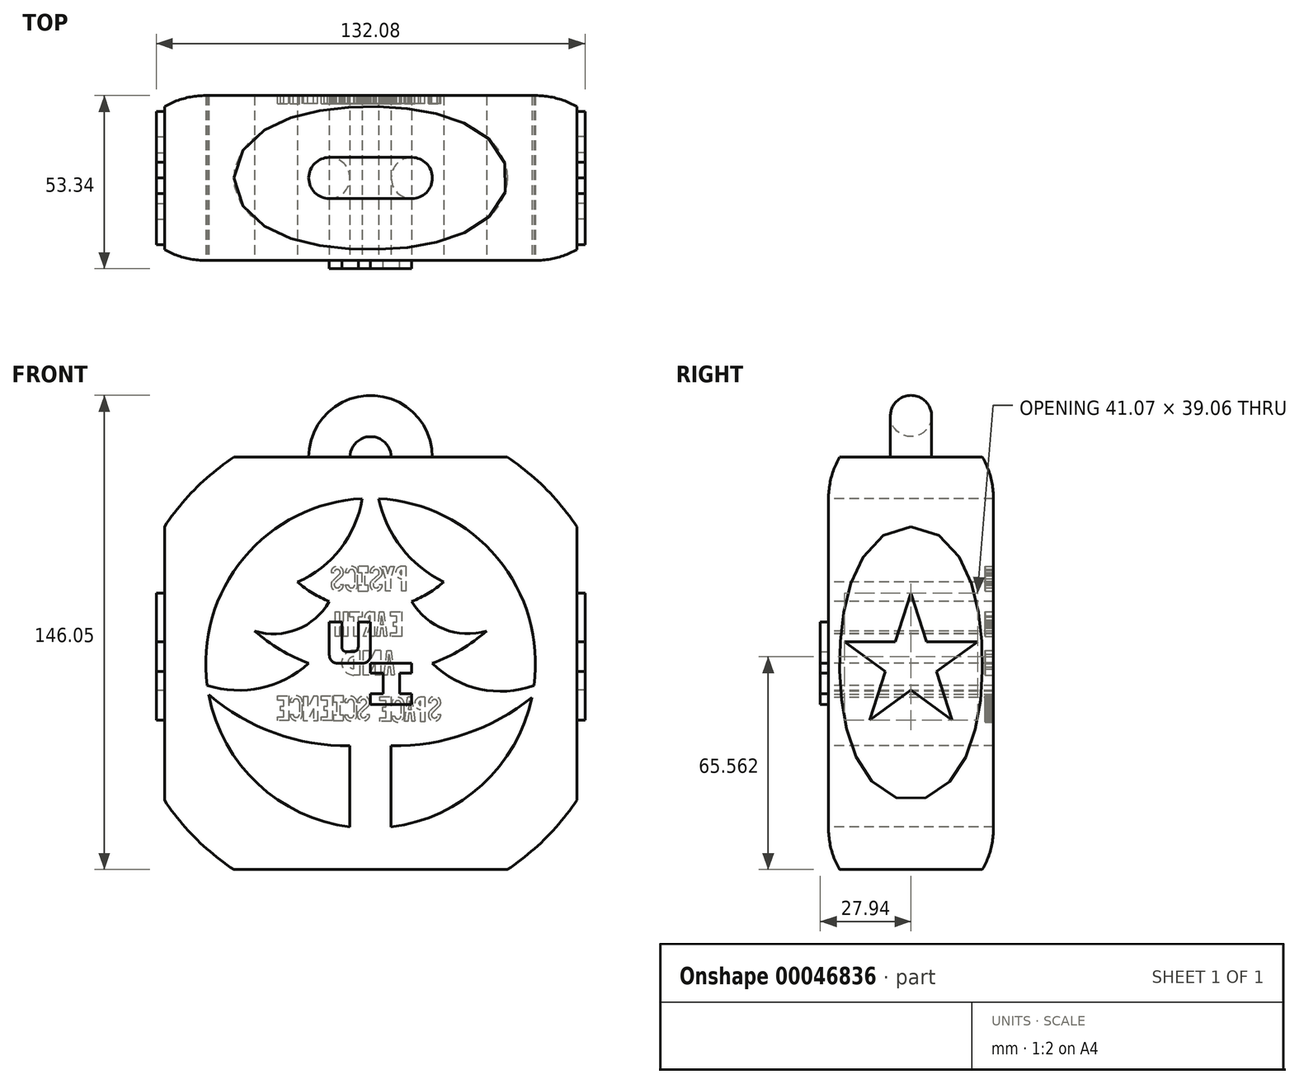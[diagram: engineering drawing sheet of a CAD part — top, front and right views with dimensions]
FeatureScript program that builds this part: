
annotation { "Feature Type Name" : "Feature", "Feature Type Description" : "" }
export const myFeature = defineFeature(function(context is Context, id is Id, definition is map)
    precondition{}
    {
        {
            var Q0;
            Q0=qCreatedBy(makeId("Top.planeOp"),FACE);
            var sketch = newSketch(context, id + "F0", { "sketchPlane" : qUnion([Q0])});
            skLineSegment(sketch, "E0", {"start": v(0, 0) * mm, "end": v(0, 25.4) * mm});
            skLineSegment(sketch, "E1", {"start": v(0, 0) * mm, "end": v(0, -25.4) * mm});
            skLineSegment(sketch, "E2", {"start": v(0, 25.4) * mm, "end": v(50.8, 25.4) * mm});
            skLineSegment(sketch, "E3", {"start": v(50.8, 25.4) * mm, "end": v(50.8, -25.4) * mm});
            skLineSegment(sketch, "E4", {"start": v(50.8, -25.4) * mm, "end": v(0, -25.4) * mm});
            skArc(sketch, "E5", {"start": v(50.8, -25.4) * mm, "mid": v(76.2, 0) * mm, "end": v(50.8, 25.4) * mm});
            skSolve(sketch);
        }
        {
            var Q0;
            Q0 = qSketchRegion(id + "F0", true);
            var Q1;
            Q1=sQuery(id+"F0.wireOp",EDGE,"E0");
            revolve(context, id + "F1", {"entities" : qUnion([Q0]), "axis" : qUnion([Q1]), "revolveType" : RevolveType.FULL});
        }
        {
            var Q0;
            Q0=makeQuery(id+"F1.opRevolve","SWEPT_FACE",FACE,{"disambiguationData":[OSD([sQuery(id+"F0.wireOp",EDGE,"E4")])]});
            var sketch = newSketch(context, id + "F2", { "sketchPlane" : qUnion([Q0])});
            skLineSegment(sketch, "E6", {"start": v(-6.35, -48.26) * mm, "end": v(-6.35, -25.4) * mm});
            skLineSegment(sketch, "E7", {"start": v(6.35, -48.26) * mm, "end": v(6.35, -25.4) * mm});
            skArc(sketch, "E8", {"start": v(19.05, 0) * mm, "mid": v(33.72, -7.94) * mm, "end": v(50.35, -6.75) * mm});
            skArc(sketch, "E9", {"start": v(-50.35, -6.75) * mm, "mid": v(-33.8, -7.59) * mm, "end": v(-19.05, 0) * mm});
            skArc(sketch, "E10", {"start": v(-35.73, 9.97) * mm, "mid": v(-27.84, 4.23) * mm, "end": v(-19.05, 0) * mm});
            skArc(sketch, "E11", {"start": v(12.7, 19.05) * mm, "mid": v(22.65, 10.55) * mm, "end": v(35.73, 9.97) * mm});
            skArc(sketch, "E12", {"start": v(-35.73, 9.97) * mm, "mid": v(-22.62, 10.46) * mm, "end": v(-12.7, 19.05) * mm});
            skArc(sketch, "E13", {"start": v(-22.52, 25.06) * mm, "mid": v(-17.86, 21.64) * mm, "end": v(-12.7, 19.05) * mm});
            skArc(sketch, "E14.trimOffspring", {"start": v(12.7, 19.05) * mm, "mid": v(17.86, 21.64) * mm, "end": v(22.52, 25.06) * mm});
            skArc(sketch, "E15.trimOffspring", {"start": v(19.05, 0) * mm, "mid": v(27.84, 4.23) * mm, "end": v(35.73, 9.97) * mm});
            skLineSegment(sketch, "E16", {"start": v(-6.35, -48.26) * mm, "end": v(-6.35, -50.4) * mm});
            skLineSegment(sketch, "E17", {"start": v(6.35, -48.26) * mm, "end": v(6.35, -50.4) * mm});
            skArc(sketch, "E18", {"start": v(-22.52, 25.06) * mm, "mid": v(-9.27, 35.35) * mm, "end": v(-2.6, 50.73) * mm});
            skArc(sketch, "E19", {"start": v(2.53, 50.74) * mm, "mid": v(9.54, 35.57) * mm, "end": v(22.52, 25.06) * mm});
            skCircle(sketch, "E20", {"center": v(0, 0) * mm, "radius": 50.8 * mm});
            skArc(sketch, "E21", {"start": v(-49.88, -9.63) * mm, "mid": v(-29.55, -21.47) * mm, "end": v(-6.35, -25.4) * mm});
            skArc(sketch, "E22", {"start": v(6.35, -25.4) * mm, "mid": v(29.33, -21.72) * mm, "end": v(49.7, -10.48) * mm});
            skSolve(sketch);
        }
        {
            var Q0;
            Q0=makeQuery(id+"F2.imprint","IMPRINT",FACE,{"disambiguationData":[TD([[makeQuery(id+"F2.imprint","IMPRINT",EDGE,{"derivedFrom":sQuery(id+"F2.wireOp",EDGE,"E6")}),1.0]])]});
            extrude(context, id + "F3", {"entities" : qUnion([Q0]), "operationType" : NewBodyOperationType.REMOVE, "oppositeDirection" : true, "depth" : 145.88 * mm});
        }
        {
            var Q0;
            {var subQ2=sQuery(id+"F2.wireOp",EDGE,"E8");Q0=makeQuery(id+"F2.imprint","IMPRINT",FACE,{"disambiguationData":[TD([[makeQuery(id+"F2.imprint","IMPRINT",EDGE,{"derivedFrom":subQ2}),1.0]])]});}
            extrude(context, id + "F4", {"entities" : qUnion([Q0]), "operationType" : NewBodyOperationType.REMOVE, "oppositeDirection" : true, "depth" : 112.84 * mm});
        }
        {
            var Q0;
            {var subQ1=sQuery(id+"F2.wireOp",EDGE,"E9");Q0=makeQuery(id+"F2.imprint","IMPRINT",FACE,{"disambiguationData":[TD([[makeQuery(id+"F2.imprint","IMPRINT",EDGE,{"derivedFrom":subQ1}),1.0]])]});}
            extrude(context, id + "F5", {"entities" : qUnion([Q0]), "operationType" : NewBodyOperationType.REMOVE, "oppositeDirection" : true, "depth" : 60.8 * mm});
        }
        {
            var Q0;
            Q0=makeQuery(id+"F2.imprint","IMPRINT",FACE,{"disambiguationData":[TD([[makeQuery(id+"F2.imprint","IMPRINT",EDGE,{"derivedFrom":sQuery(id+"F2.wireOp",EDGE,"E7")}),-1.0]])]});
            extrude(context, id + "F6", {"entities" : qUnion([Q0]), "operationType" : NewBodyOperationType.REMOVE, "oppositeDirection" : true, "depth" : 63.8 * mm});
        }
        {
            var Q0;
            Q0=makeQuery(id+"F1.opRevolve","SWEPT_FACE",FACE,{"disambiguationData":[OSD([sQuery(id+"F0.wireOp",EDGE,"E4")])]});
            var sketch = newSketch(context, id + "F7", { "sketchPlane" : qUnion([Q0])});
            skLineSegment(sketch, "E23", {"start": v(0, 0) * mm, "end": v(0, -63.5) * mm});
            skPoint(sketch, "E23.endSnap0", {"position": v(0, -50.8) * mm});
            skLineSegment(sketch, "E24", {"start": v(0, -63.5) * mm, "end": v(-69.31, -63.5) * mm});
            skLineSegment(sketch, "E25", {"start": v(-69.31, -63.5) * mm, "end": v(-69.31, -78.3) * mm});
            skLineSegment(sketch, "E26", {"start": v(-69.31, -78.3) * mm, "end": v(74.16, -78.3) * mm});
            skLineSegment(sketch, "E27", {"start": v(74.16, -78.3) * mm, "end": v(74.16, -63.5) * mm});
            skLineSegment(sketch, "E28", {"start": v(74.16, -63.5) * mm, "end": v(0, -63.5) * mm});
            skLineSegment(sketch, "E29", {"start": v(0, 0) * mm, "end": v(-63.5, 0) * mm});
            skLineSegment(sketch, "E30", {"start": v(0, 0) * mm, "end": v(63.5, 0) * mm});
            skLineSegment(sketch, "E31", {"start": v(0, 0) * mm, "end": v(0, 63.5) * mm});
            skLineSegment(sketch, "E32", {"start": v(-63.5, 0) * mm, "end": v(-63.5, 51.43) * mm});
            skLineSegment(sketch, "E33", {"start": v(-63.5, 51.43) * mm, "end": v(-82.24, 51.43) * mm});
            skLineSegment(sketch, "E34", {"start": v(-82.24, 51.43) * mm, "end": v(-82.24, -30.11) * mm});
            skLineSegment(sketch, "E35", {"start": v(-82.24, -30.11) * mm, "end": v(-82.24, -49.77) * mm});
            skLineSegment(sketch, "E36", {"start": v(-82.24, -49.77) * mm, "end": v(-63.5, -49.77) * mm});
            skLineSegment(sketch, "E37", {"start": v(-63.5, -49.77) * mm, "end": v(-63.5, 0) * mm});
            skLineSegment(sketch, "E38", {"start": v(63.5, 0) * mm, "end": v(63.5, 56.35) * mm});
            skLineSegment(sketch, "E39", {"start": v(63.5, 56.35) * mm, "end": v(89.23, 56.35) * mm});
            skLineSegment(sketch, "E40", {"start": v(89.23, 56.35) * mm, "end": v(89.23, -52.38) * mm});
            skLineSegment(sketch, "E41", {"start": v(89.23, -52.38) * mm, "end": v(63.5, -52.38) * mm});
            skLineSegment(sketch, "E42", {"start": v(63.5, -52.38) * mm, "end": v(63.5, 0) * mm});
            skLineSegment(sketch, "E43", {"start": v(0, 63.5) * mm, "end": v(48.36, 63.5) * mm});
            skLineSegment(sketch, "E44", {"start": v(48.36, 63.5) * mm, "end": v(48.36, 80.87) * mm});
            skLineSegment(sketch, "E45", {"start": v(48.36, 80.87) * mm, "end": v(-58.03, 80.87) * mm});
            skLineSegment(sketch, "E46", {"start": v(-58.03, 80.87) * mm, "end": v(-58.03, 63.5) * mm});
            skLineSegment(sketch, "E47", {"start": v(-58.03, 63.5) * mm, "end": v(0, 63.5) * mm});
            skSolve(sketch);
        }
        {
            var Q0;
            Q0 = qSketchRegion(id + "F7", true);
            extrude(context, id + "F8", {"entities" : qUnion([Q0]), "operationType" : NewBodyOperationType.REMOVE, "oppositeDirection" : true, "depth" : 73.08 * mm});
        }
        {
            var Q0;
            Q0 = qSketchRegion(id + "F7", true);
            extrude(context, id + "F9", {"entities" : qUnion([Q0]), "operationType" : NewBodyOperationType.REMOVE, "oppositeDirection" : true, "depth" : 74.54 * mm});
        }
        {
            var Q0;
            Q0=makeQuery(id+"F8.boolean.opBoolean","COPY",FACE,{"derivedFrom":makeQuery(id+"F8.opExtrude","SWEPT_FACE",FACE,{"disambiguationData":[OSD([sQuery(id+"F7.wireOp",EDGE,"E43"),sQuery(id+"F7.wireOp",EDGE,"E47")])]})});
            var sketch = newSketch(context, id + "F10", { "sketchPlane" : qUnion([Q0])});
            skLineSegment(sketch, "E48", {"start": v(0, 0) * mm, "end": v(12.7, 0) * mm});
            skLineSegment(sketch, "E49", {"start": v(0, 0) * mm, "end": v(0, 12.46) * mm});
            skLineSegment(sketch, "E50", {"start": v(0, 0) * mm, "end": v(-12.7, 0) * mm});
            skCircle(sketch, "E51", {"center": v(12.7, 0) * mm, "radius": 6.35 * mm});
            skCircle(sketch, "E52", {"center": v(-12.7, 0) * mm, "radius": 6.35 * mm});
            skSolve(sketch);
        }
        {
            var Q0;
            Q0=makeQuery(id+"F10.imprint","IMPRINT",FACE,{"disambiguationData":[TD([[makeQuery(id+"F10.imprint","IMPRINT",EDGE,{"derivedFrom":sQuery(id+"F10.wireOp",EDGE,"E52")}),1.0]])]});
            var Q1;
            Q1=sQuery(id+"F10.wireOp",EDGE,"E49");
            revolve(context, id + "F11", {"operationType" : NewBodyOperationType.ADD, "entities" : qUnion([Q0]), "axis" : qUnion([Q1]), "revolveType" : RevolveType.ONE_DIRECTION, "angle" : 180 * degree});
        }
        {
            var Q0;
            Q0=makeQuery(id+"F8.boolean.opBoolean","COPY",FACE,{"derivedFrom":makeQuery(id+"F8.opExtrude","SWEPT_FACE",FACE,{"disambiguationData":[OSD([sQuery(id+"F7.wireOp",EDGE,"E32"),sQuery(id+"F7.wireOp",EDGE,"E37")])]})});
            var sketch = newSketch(context, id + "F12", { "sketchPlane" : qUnion([Q0])});
            skLineSegment(sketch, "E53", {"start": v(0, 21.59) * mm, "end": v(-4.85, 6.67) * mm});
            skLineSegment(sketch, "E54", {"start": v(20.53, 6.67) * mm, "end": v(7.84, -2.55) * mm});
            skLineSegment(sketch, "E55", {"start": v(-20.53, 6.67) * mm, "end": v(-4.85, 6.67) * mm});
            skLineSegment(sketch, "E56", {"start": v(-20.53, 6.67) * mm, "end": v(-7.84, -2.55) * mm});
            skLineSegment(sketch, "E57", {"start": v(12.7, -17.47) * mm, "end": v(7.84, -2.55) * mm});
            skLineSegment(sketch, "E58.trimOffspring", {"start": v(4.85, 6.67) * mm, "end": v(20.53, 6.67) * mm});
            skLineSegment(sketch, "E59.trimOffspring", {"start": v(4.85, 6.67) * mm, "end": v(0, 21.59) * mm});
            skLineSegment(sketch, "E60.trimOffspring", {"start": v(0, -8.25) * mm, "end": v(-12.7, -17.47) * mm});
            skLineSegment(sketch, "E61.trimOffspring", {"start": v(0, -8.25) * mm, "end": v(12.7, -17.47) * mm});
            skLineSegment(sketch, "E62.trimOffspring", {"start": v(-7.84, -2.55) * mm, "end": v(-12.7, -17.47) * mm});
            skSolve(sketch);
        }
        {
            var Q0;
            Q0 = qSketchRegion(id + "F12", true);
            extrude(context, id + "F13", {"entities" : qUnion([Q0]), "operationType" : NewBodyOperationType.ADD, "depth" : 2.54 * mm});
        }
        {
            var Q0;
            Q0=makeQuery(id+"F8.boolean.opBoolean","COPY",FACE,{"derivedFrom":makeQuery(id+"F8.opExtrude","SWEPT_FACE",FACE,{"disambiguationData":[OSD([sQuery(id+"F7.wireOp",EDGE,"E38"),sQuery(id+"F7.wireOp",EDGE,"E42")])]})});
            var sketch = newSketch(context, id + "F14", { "sketchPlane" : qUnion([Q0])});
            skCircle(sketch, "E63.cCircle", {"center": v(0, 0) * mm, "radius": 21.59 * mm, "construction": true});
            skLineSegment(sketch, "E63.0", {"start": v(0, 21.59) * mm, "end": v(20.53, 6.67) * mm});
            skLineSegment(sketch, "E63.1", {"start": v(20.53, 6.67) * mm, "end": v(12.7, -17.47) * mm});
            skLineSegment(sketch, "E63.2", {"start": v(12.7, -17.47) * mm, "end": v(-12.7, -17.47) * mm});
            skLineSegment(sketch, "E63.3", {"start": v(-12.7, -17.47) * mm, "end": v(-20.53, 6.67) * mm});
            skLineSegment(sketch, "E63.4", {"start": v(-20.53, 6.67) * mm, "end": v(0, 21.59) * mm});
            skLineSegment(sketch, "E64", {"start": v(-12.7, -17.47) * mm, "end": v(-7.84, -2.55) * mm});
            skLineSegment(sketch, "E65", {"start": v(12.7, -17.47) * mm, "end": v(7.84, -2.55) * mm});
            skLineSegment(sketch, "E66", {"start": v(-20.53, 6.67) * mm, "end": v(-4.85, 6.67) * mm});
            skLineSegment(sketch, "E67", {"start": v(20.53, 6.67) * mm, "end": v(7.84, -2.55) * mm});
            skLineSegment(sketch, "E68", {"start": v(-20.53, 6.67) * mm, "end": v(-7.84, -2.55) * mm});
            skLineSegment(sketch, "E69.trimOffspring", {"start": v(4.85, 6.67) * mm, "end": v(20.53, 6.67) * mm});
            skLineSegment(sketch, "E70.trimOffspring", {"start": v(4.85, 6.67) * mm, "end": v(0, 21.59) * mm});
            skLineSegment(sketch, "E71.trimOffspring", {"start": v(0, -8.25) * mm, "end": v(-12.7, -17.47) * mm});
            skLineSegment(sketch, "E72.trimOffspring", {"start": v(0, -8.25) * mm, "end": v(12.7, -17.47) * mm});
            skLineSegment(sketch, "E73.trimOffspring", {"start": v(-4.85, 6.67) * mm, "end": v(0, 21.59) * mm});
            skSolve(sketch);
        }
        {
            var Q0;
            Q0=makeQuery(id+"F14.imprint","IMPRINT",FACE,{"disambiguationData":[TD([[makeQuery(id+"F14.imprint","IMPRINT",EDGE,{"derivedFrom":sQuery(id+"F14.wireOp",EDGE,"E64")}),-1.0]])]});
            extrude(context, id + "F15", {"entities" : qUnion([Q0]), "operationType" : NewBodyOperationType.ADD, "depth" : 2.54 * mm});
        }
        {
            var Q0;
            Q0=makeQuery(id+"F1.opRevolve","SWEPT_FACE",FACE,{"disambiguationData":[OSD([sQuery(id+"F0.wireOp",EDGE,"E4")])]});
            var sketch = newSketch(context, id + "F16", { "sketchPlane" : qUnion([Q0])});
            skLineSegment(sketch, "E74", {"start": v(-2.54, 0) * mm, "end": v(-10.16, 0) * mm});
            skLineSegment(sketch, "E75", {"start": v(-12.7, 2.54) * mm, "end": v(-12.7, 12.7) * mm});
            skLineSegment(sketch, "E76", {"start": v(-12.7, 12.7) * mm, "end": v(-8.9, 12.7) * mm});
            skLineSegment(sketch, "E77", {"start": v(-8.9, 12.7) * mm, "end": v(-8.9, 5.08) * mm});
            skLineSegment(sketch, "E78", {"start": v(-7.37, 3.56) * mm, "end": v(-5.33, 3.56) * mm});
            skLineSegment(sketch, "E79", {"start": v(-3.8, 5.08) * mm, "end": v(-3.8, 12.7) * mm});
            skLineSegment(sketch, "E80", {"start": v(-3.81, 12.7) * mm, "end": v(0, 12.7) * mm});
            skLineSegment(sketch, "E81", {"start": v(0, 12.7) * mm, "end": v(0, 2.54) * mm});
            skPoint(sketch, "E82.visualSharp", {"position": v(-8.9, 3.56) * mm});
            skArc(sketch, "E82.filletArc", {"start": v(-8.9, 5.08) * mm, "mid": v(-8.44, 4) * mm, "end": v(-7.37, 3.56) * mm});
            skPoint(sketch, "E83.visualSharp", {"position": v(-3.8, 3.56) * mm});
            skArc(sketch, "E83.filletArc", {"start": v(-5.33, 3.56) * mm, "mid": v(-4.26, 4) * mm, "end": v(-3.8, 5.08) * mm});
            skPoint(sketch, "E84.visualSharp", {"position": v(-12.7, 0) * mm});
            skArc(sketch, "E84.filletArc", {"start": v(-12.7, 2.54) * mm, "mid": v(-11.96, 0.74) * mm, "end": v(-10.16, 0) * mm});
            skPoint(sketch, "E85.visualSharp", {"position": v(0, 0) * mm});
            skArc(sketch, "E85.filletArc", {"start": v(-2.54, 0) * mm, "mid": v(-0.74, 0.74) * mm, "end": v(0, 2.54) * mm});
            skLineSegment(sketch, "E86", {"start": v(0, 0) * mm, "end": v(12.7, 0) * mm});
            skLineSegment(sketch, "E87", {"start": v(0, 0) * mm, "end": v(0, -3.05) * mm});
            skLineSegment(sketch, "E88", {"start": v(0, -3.05) * mm, "end": v(3.8, -3.05) * mm});
            skLineSegment(sketch, "E89", {"start": v(3.81, -3.05) * mm, "end": v(3.81, -9.4) * mm});
            skLineSegment(sketch, "E90", {"start": v(3.81, -9.4) * mm, "end": v(0, -9.4) * mm});
            skLineSegment(sketch, "E91", {"start": v(0, -9.4) * mm, "end": v(0, -12.7) * mm});
            skLineSegment(sketch, "E92", {"start": v(0, -12.7) * mm, "end": v(12.7, -12.7) * mm});
            skLineSegment(sketch, "E93", {"start": v(12.7, -12.7) * mm, "end": v(12.7, -9.4) * mm});
            skLineSegment(sketch, "E94", {"start": v(12.7, -9.4) * mm, "end": v(8.9, -9.4) * mm});
            skLineSegment(sketch, "E95", {"start": v(8.9, -9.4) * mm, "end": v(8.9, -3.05) * mm});
            skLineSegment(sketch, "E96", {"start": v(8.9, -3.05) * mm, "end": v(12.7, -3.05) * mm});
            skLineSegment(sketch, "E97", {"start": v(12.7, -3.05) * mm, "end": v(12.7, 0) * mm});
            skSolve(sketch);
        }
        {
            var Q0;
            Q0 = qSketchRegion(id + "F16", true);
            extrude(context, id + "F17", {"entities" : qUnion([Q0]), "operationType" : NewBodyOperationType.ADD, "depth" : 2.54 * mm});
        }
        {
            var Q0;
            Q0=makeQuery(id+"F1.opRevolve","SWEPT_FACE",FACE,{"disambiguationData":[OSD([sQuery(id+"F0.wireOp",EDGE,"E2")])]});
            var sketch = newSketch(context, id + "F18", { "sketchPlane" : qUnion([Q0])});
            skLineSegment(sketch, "E98", {"start": v(-10.91, 29.9) * mm, "end": v(-10.91, 22.27) * mm});
            skLineSegment(sketch, "E99", {"start": v(-10.91, 22.27) * mm, "end": v(-9.64, 22.27) * mm});
            skLineSegment(sketch, "E100", {"start": v(-9.64, 22.27) * mm, "end": v(-9.64, 26.08) * mm});
            skLineSegment(sketch, "E101", {"start": v(-10.91, 29.9) * mm, "end": v(-9.64, 29.9) * mm});
            skArc(sketch, "E102", {"start": v(-9.64, 26.08) * mm, "mid": v(-7.74, 27.99) * mm, "end": v(-9.64, 29.9) * mm});
            skLineSegment(sketch, "E103", {"start": v(-9.64, 27.35) * mm, "end": v(-9.64, 28.62) * mm});
            skArc(sketch, "E104", {"start": v(-9.64, 27.35) * mm, "mid": v(-9, 27.99) * mm, "end": v(-9.64, 28.62) * mm});
            skLineSegment(sketch, "E105", {"start": v(-7.24, 29.9) * mm, "end": v(-6.15, 26.08) * mm});
            skLineSegment(sketch, "E106", {"start": v(-6.15, 26.08) * mm, "end": v(-6.15, 22.27) * mm});
            skLineSegment(sketch, "E107", {"start": v(-6.15, 22.27) * mm, "end": v(-4.68, 22.27) * mm});
            skLineSegment(sketch, "E108", {"start": v(-4.68, 22.27) * mm, "end": v(-4.68, 26.08) * mm});
            skLineSegment(sketch, "E109", {"start": v(-4.68, 26.08) * mm, "end": v(-3.49, 29.9) * mm});
            skLineSegment(sketch, "E110", {"start": v(-3.49, 29.9) * mm, "end": v(-4.58, 29.9) * mm});
            skLineSegment(sketch, "E111", {"start": v(-4.58, 29.9) * mm, "end": v(-5.28, 27.55) * mm});
            skLineSegment(sketch, "E112", {"start": v(-5.28, 27.55) * mm, "end": v(-6.08, 29.9) * mm});
            skLineSegment(sketch, "E113", {"start": v(-6.08, 29.9) * mm, "end": v(-7.24, 29.9) * mm});
            skPoint(sketch, "E114.endSnap0", {"position": v(-4.08, 27.99) * mm});
            skArc(sketch, "E115", {"start": v(0.19, 27.99) * mm, "mid": v(-2.24, 29.82) * mm, "end": v(-3.33, 26.97) * mm});
            skLineSegment(sketch, "E116", {"start": v(0.19, 27.99) * mm, "end": v(-0.78, 27.99) * mm});
            skArc(sketch, "E117", {"start": v(-0.78, 27.99) * mm, "mid": v(-1.95, 28.9) * mm, "end": v(-2.54, 27.53) * mm});
            skArc(sketch, "E118", {"start": v(-3.62, 24.18) * mm, "mid": v(-1.12, 22.37) * mm, "end": v(-0.19, 25.3) * mm});
            skLineSegment(sketch, "E119", {"start": v(-3.62, 24.18) * mm, "end": v(-2.66, 24.18) * mm});
            skArc(sketch, "E120", {"start": v(-2.66, 24.18) * mm, "mid": v(-1.46, 23.27) * mm, "end": v(-0.92, 24.68) * mm});
            skLineSegment(sketch, "E121", {"start": v(-3.33, 26.97) * mm, "end": v(-0.92, 24.68) * mm});
            skLineSegment(sketch, "E122", {"start": v(-2.54, 27.53) * mm, "end": v(-0.19, 25.3) * mm});
            skPoint(sketch, "E114.start.orphan", {"position": v(-1.72, 29.9) * mm});
            skPoint(sketch, "E123.start.orphan", {"position": v(-1.72, 22.27) * mm});
            skLineSegment(sketch, "E124", {"start": v(0.68, 27.99) * mm, "end": v(0.68, 29.9) * mm});
            skLineSegment(sketch, "E125", {"start": v(0.68, 29.9) * mm, "end": v(3.84, 29.9) * mm});
            skLineSegment(sketch, "E126", {"start": v(3.84, 29.9) * mm, "end": v(3.84, 27.99) * mm});
            skLineSegment(sketch, "E127", {"start": v(3.84, 27.99) * mm, "end": v(2.8, 27.99) * mm});
            skLineSegment(sketch, "E128", {"start": v(2.8, 27.99) * mm, "end": v(2.8, 24) * mm});
            skLineSegment(sketch, "E129", {"start": v(2.8, 24) * mm, "end": v(3.84, 24) * mm});
            skLineSegment(sketch, "E130", {"start": v(3.84, 24) * mm, "end": v(3.84, 22.27) * mm});
            skLineSegment(sketch, "E131", {"start": v(3.84, 22.27) * mm, "end": v(0.68, 22.27) * mm});
            skLineSegment(sketch, "E132", {"start": v(0.68, 22.27) * mm, "end": v(0.68, 24) * mm});
            skLineSegment(sketch, "E133", {"start": v(0.68, 24) * mm, "end": v(1.69, 24) * mm});
            skLineSegment(sketch, "E134", {"start": v(1.69, 24) * mm, "end": v(1.69, 27.99) * mm});
            skLineSegment(sketch, "E135", {"start": v(1.69, 27.99) * mm, "end": v(0.68, 27.99) * mm});
            skArc(sketch, "E136", {"start": v(7.77, 27.99) * mm, "mid": v(5.86, 29.9) * mm, "end": v(3.96, 27.99) * mm});
            skArc(sketch, "E137", {"start": v(3.96, 24.18) * mm, "mid": v(5.86, 22.27) * mm, "end": v(7.77, 24.18) * mm});
            skLineSegment(sketch, "E138", {"start": v(7.77, 27.99) * mm, "end": v(6.8, 27.99) * mm});
            skArc(sketch, "E139", {"start": v(6.8, 27.99) * mm, "mid": v(5.86, 28.92) * mm, "end": v(4.92, 27.99) * mm});
            skLineSegment(sketch, "E140", {"start": v(7.77, 24.18) * mm, "end": v(6.8, 24.18) * mm});
            skArc(sketch, "E141", {"start": v(4.92, 24.18) * mm, "mid": v(5.86, 23.24) * mm, "end": v(6.8, 24.18) * mm});
            skLineSegment(sketch, "E142", {"start": v(3.96, 24.18) * mm, "end": v(3.96, 27.99) * mm});
            skLineSegment(sketch, "E143", {"start": v(4.92, 27.99) * mm, "end": v(4.92, 24.18) * mm});
            skPoint(sketch, "E144.end.orphan", {"position": v(5.86, 29.9) * mm});
            skLineSegment(sketch, "E145", {"start": v(12.18, 28) * mm, "end": v(11.22, 28) * mm});
            skLineSegment(sketch, "E146", {"start": v(9.46, 27.55) * mm, "end": v(11.81, 25.33) * mm});
            skArc(sketch, "E147", {"start": v(11.22, 28) * mm, "mid": v(10.04, 28.92) * mm, "end": v(9.46, 27.55) * mm});
            skLineSegment(sketch, "E148", {"start": v(8.67, 27) * mm, "end": v(11.07, 24.7) * mm});
            skArc(sketch, "E149", {"start": v(9.34, 24.2) * mm, "mid": v(10.54, 23.3) * mm, "end": v(11.07, 24.7) * mm});
            skArc(sketch, "E150", {"start": v(12.18, 28) * mm, "mid": v(9.75, 29.84) * mm, "end": v(8.67, 27) * mm});
            skArc(sketch, "E151", {"start": v(8.37, 24.2) * mm, "mid": v(10.88, 22.39) * mm, "end": v(11.81, 25.33) * mm});
            skPoint(sketch, "E152.start.orphan", {"position": v(10.28, 22.3) * mm});
            skPoint(sketch, "E153.start.orphan", {"position": v(10.28, 29.91) * mm});
            skLineSegment(sketch, "E154", {"start": v(8.37, 24.2) * mm, "end": v(9.34, 24.2) * mm});
            skLineSegment(sketch, "E155", {"start": v(0, 15.96) * mm, "end": v(-1.17, 15.96) * mm});
            skLineSegment(sketch, "E156", {"start": v(-1.17, 15.96) * mm, "end": v(-1.17, 8.34) * mm});
            skLineSegment(sketch, "E157", {"start": v(-1.17, 8.34) * mm, "end": v(0, 8.34) * mm});
            skLineSegment(sketch, "E158", {"start": v(0, 8.34) * mm, "end": v(-0.04, 12.15) * mm});
            skLineSegment(sketch, "E159", {"start": v(-0.04, 12.15) * mm, "end": v(1.25, 8.34) * mm});
            skLineSegment(sketch, "E160", {"start": v(1.25, 8.34) * mm, "end": v(2.18, 8.34) * mm});
            skArc(sketch, "E161", {"start": v(0.82, 12.33) * mm, "mid": v(1.86, 14.47) * mm, "end": v(0, 15.96) * mm});
            skLineSegment(sketch, "E162", {"start": v(2.18, 8.34) * mm, "end": v(0.82, 12.33) * mm});
            skLineSegment(sketch, "E163", {"start": v(0, 13.42) * mm, "end": v(0, 14.69) * mm});
            skArc(sketch, "E164", {"start": v(0, 13.42) * mm, "mid": v(0.66, 14.05) * mm, "end": v(0, 14.69) * mm});
            skLineSegment(sketch, "E165", {"start": v(-1.9, 8.34) * mm, "end": v(-2.79, 15.96) * mm});
            skLineSegment(sketch, "E166", {"start": v(-2.79, 15.96) * mm, "end": v(-4, 15.96) * mm});
            skLineSegment(sketch, "E167", {"start": v(-4, 15.96) * mm, "end": v(-5.04, 8.34) * mm});
            skLineSegment(sketch, "E168", {"start": v(-5.04, 8.34) * mm, "end": v(-4.1, 8.34) * mm});
            skLineSegment(sketch, "E169", {"start": v(-4.1, 8.34) * mm, "end": v(-3.84, 10.86) * mm});
            skLineSegment(sketch, "E170", {"start": v(-3.84, 10.86) * mm, "end": v(-3.05, 10.86) * mm});
            skLineSegment(sketch, "E171", {"start": v(-3.05, 10.86) * mm, "end": v(-2.85, 8.34) * mm});
            skLineSegment(sketch, "E172", {"start": v(-2.85, 8.34) * mm, "end": v(-1.9, 8.34) * mm});
            skLineSegment(sketch, "E173", {"start": v(-3.84, 11.88) * mm, "end": v(-3.05, 11.89) * mm});
            skLineSegment(sketch, "E174", {"start": v(-3.05, 11.89) * mm, "end": v(-3.4, 14.7) * mm});
            skPoint(sketch, "E174.endSnap0", {"position": v(-3.4, 15.96) * mm});
            skLineSegment(sketch, "E175", {"start": v(-3.4, 14.7) * mm, "end": v(-3.84, 11.88) * mm});
            skLineSegment(sketch, "E176", {"start": v(-6.17, 15.96) * mm, "end": v(-9.59, 15.96) * mm});
            skLineSegment(sketch, "E177", {"start": v(-9.59, 15.96) * mm, "end": v(-9.59, 8.34) * mm});
            skLineSegment(sketch, "E178", {"start": v(-9.59, 8.34) * mm, "end": v(-6.17, 8.34) * mm});
            skLineSegment(sketch, "E179", {"start": v(-6.17, 8.34) * mm, "end": v(-6.17, 9.43) * mm});
            skLineSegment(sketch, "E180", {"start": v(-6.17, 9.43) * mm, "end": v(-8.1, 9.43) * mm});
            skLineSegment(sketch, "E181", {"start": v(-8.1, 9.43) * mm, "end": v(-8.1, 11.36) * mm});
            skLineSegment(sketch, "E182", {"start": v(-8.1, 11.36) * mm, "end": v(-7.07, 11.36) * mm});
            skLineSegment(sketch, "E183", {"start": v(-7.07, 11.36) * mm, "end": v(-7.07, 12.78) * mm});
            skLineSegment(sketch, "E184", {"start": v(-7.07, 12.78) * mm, "end": v(-8.1, 12.78) * mm});
            skLineSegment(sketch, "E185", {"start": v(-8.1, 12.78) * mm, "end": v(-8.1, 14.59) * mm});
            skLineSegment(sketch, "E186", {"start": v(-8.1, 14.59) * mm, "end": v(-6.17, 14.59) * mm});
            skLineSegment(sketch, "E187", {"start": v(-6.17, 14.59) * mm, "end": v(-6.17, 15.96) * mm});
            skLineSegment(sketch, "E188", {"start": v(2.6, 15.96) * mm, "end": v(2.6, 14.27) * mm});
            skLineSegment(sketch, "E189", {"start": v(2.6, 14.27) * mm, "end": v(3.86, 14.27) * mm});
            skLineSegment(sketch, "E190", {"start": v(3.86, 14.27) * mm, "end": v(3.86, 8.34) * mm});
            skLineSegment(sketch, "E191", {"start": v(3.86, 8.34) * mm, "end": v(5.13, 8.34) * mm});
            skLineSegment(sketch, "E192", {"start": v(5.13, 8.34) * mm, "end": v(5.13, 14.27) * mm});
            skLineSegment(sketch, "E193", {"start": v(5.13, 14.27) * mm, "end": v(6.4, 14.27) * mm});
            skLineSegment(sketch, "E194", {"start": v(6.4, 14.27) * mm, "end": v(6.4, 15.96) * mm});
            skLineSegment(sketch, "E195", {"start": v(6.4, 15.96) * mm, "end": v(2.6, 15.96) * mm});
            skLineSegment(sketch, "E196", {"start": v(6.99, 15.96) * mm, "end": v(6.99, 8.34) * mm});
            skLineSegment(sketch, "E197", {"start": v(6.99, 8.34) * mm, "end": v(8.26, 8.34) * mm});
            skLineSegment(sketch, "E198", {"start": v(8.26, 8.34) * mm, "end": v(8.26, 11.24) * mm});
            skLineSegment(sketch, "E199", {"start": v(8.26, 11.24) * mm, "end": v(9.53, 11.24) * mm});
            skLineSegment(sketch, "E200", {"start": v(9.53, 11.24) * mm, "end": v(9.53, 8.34) * mm});
            skLineSegment(sketch, "E201", {"start": v(9.53, 8.34) * mm, "end": v(10.8, 8.34) * mm});
            skLineSegment(sketch, "E202", {"start": v(10.8, 8.34) * mm, "end": v(10.8, 15.96) * mm});
            skLineSegment(sketch, "E203", {"start": v(10.8, 15.96) * mm, "end": v(9.53, 15.96) * mm});
            skLineSegment(sketch, "E204", {"start": v(9.53, 15.96) * mm, "end": v(9.53, 12.95) * mm});
            skLineSegment(sketch, "E205", {"start": v(9.53, 12.95) * mm, "end": v(8.26, 12.95) * mm});
            skLineSegment(sketch, "E206", {"start": v(8.26, 12.95) * mm, "end": v(8.26, 15.96) * mm});
            skLineSegment(sketch, "E207", {"start": v(8.26, 15.96) * mm, "end": v(6.99, 15.96) * mm});
            skLineSegment(sketch, "E208", {"start": v(-3.15, 4) * mm, "end": v(-3.15, -3.61) * mm});
            skLineSegment(sketch, "E209", {"start": v(-3.15, -3.61) * mm, "end": v(-1.37, -3.61) * mm});
            skLineSegment(sketch, "E210", {"start": v(0.4, -3.61) * mm, "end": v(2.19, -3.61) * mm});
            skLineSegment(sketch, "E211", {"start": v(2.19, -3.61) * mm, "end": v(2.19, 4) * mm});
            skLineSegment(sketch, "E212", {"start": v(2.19, 4) * mm, "end": v(0.4, 4) * mm});
            skLineSegment(sketch, "E213", {"start": v(-3.15, 4) * mm, "end": v(-1.37, 4) * mm});
            skLineSegment(sketch, "E214", {"start": v(-1.37, 0.2) * mm, "end": v(0.4, -3.61) * mm});
            skLineSegment(sketch, "E215", {"start": v(-1.37, 4) * mm, "end": v(0.4, 0.2) * mm});
            skLineSegment(sketch, "E216", {"start": v(0.4, 4) * mm, "end": v(0.4, 0.2) * mm});
            skLineSegment(sketch, "E217", {"start": v(-1.37, 0.2) * mm, "end": v(-1.37, -3.61) * mm});
            skLineSegment(sketch, "E218", {"start": v(3.34, 4) * mm, "end": v(3.34, -3.61) * mm});
            skLineSegment(sketch, "E219", {"start": v(3.34, -3.61) * mm, "end": v(5.12, -3.61) * mm});
            skLineSegment(sketch, "E220", {"start": v(3.34, 4) * mm, "end": v(5.12, 4) * mm});
            skArc(sketch, "E221", {"start": v(5.12, -3.61) * mm, "mid": v(8.93, 0.2) * mm, "end": v(5.12, 4) * mm});
            skLineSegment(sketch, "E222", {"start": v(5.12, -1.67) * mm, "end": v(5.12, 2.06) * mm});
            skArc(sketch, "E223.trimOffspring", {"start": v(5.12, -1.67) * mm, "mid": v(6.99, 0.2) * mm, "end": v(5.12, 2.06) * mm});
            skLineSegment(sketch, "E224", {"start": v(5.12, 0.2) * mm, "end": v(-5.73, 0.2) * mm});
            skLineSegment(sketch, "E225", {"start": v(-6.4, -3.57) * mm, "end": v(-6.14, -1.05) * mm});
            skLineSegment(sketch, "E226", {"start": v(-6.14, -1.05) * mm, "end": v(-5.35, -1.05) * mm});
            skPoint(sketch, "E227.endSnap0", {"position": v(-5.7, 4.05) * mm});
            skLineSegment(sketch, "E228", {"start": v(-5.35, -1.05) * mm, "end": v(-5.15, -3.57) * mm});
            skLineSegment(sketch, "E229", {"start": v(-5.7, 2.79) * mm, "end": v(-6.14, -0.03) * mm});
            skLineSegment(sketch, "E230", {"start": v(-6.14, -0.03) * mm, "end": v(-5.35, -0.03) * mm});
            skLineSegment(sketch, "E227", {"start": v(-5.35, -0.03) * mm, "end": v(-5.7, 2.79) * mm});
            skLineSegment(sketch, "E231", {"start": v(-5.08, 4.05) * mm, "end": v(-6.3, 4.05) * mm});
            skLineSegment(sketch, "E232", {"start": v(-4.2, -3.57) * mm, "end": v(-5.08, 4.05) * mm});
            skLineSegment(sketch, "E233", {"start": v(-6.3, 4.05) * mm, "end": v(-7.33, -3.57) * mm});
            skLineSegment(sketch, "E234", {"start": v(-5.15, -3.57) * mm, "end": v(-4.2, -3.57) * mm});
            skLineSegment(sketch, "E235", {"start": v(-7.33, -3.57) * mm, "end": v(-6.4, -3.57) * mm});
            skLineSegment(sketch, "E236", {"start": v(-21.31, -13.08) * mm, "end": v(-18.9, -15.38) * mm});
            skPoint(sketch, "E237.start.orphan", {"position": v(-19.7, -10.16) * mm});
            skArc(sketch, "E238", {"start": v(-20.64, -15.88) * mm, "mid": v(-19.44, -16.78) * mm, "end": v(-18.9, -15.38) * mm});
            skArc(sketch, "E239", {"start": v(-17.8, -12.07) * mm, "mid": v(-20.22, -10.24) * mm, "end": v(-21.31, -13.08) * mm});
            skLineSegment(sketch, "E240", {"start": v(-20.52, -12.52) * mm, "end": v(-18.17, -14.75) * mm});
            skArc(sketch, "E241", {"start": v(-21.6, -15.88) * mm, "mid": v(-19.1, -17.69) * mm, "end": v(-18.17, -14.75) * mm});
            skArc(sketch, "E242", {"start": v(-18.76, -12.07) * mm, "mid": v(-19.93, -11.16) * mm, "end": v(-20.52, -12.52) * mm});
            skPoint(sketch, "E243.start.orphan", {"position": v(-19.7, -17.78) * mm});
            skLineSegment(sketch, "E244", {"start": v(-17.8, -12.07) * mm, "end": v(-18.76, -12.07) * mm});
            skLineSegment(sketch, "E245", {"start": v(-21.6, -15.88) * mm, "end": v(-20.64, -15.88) * mm});
            skLineSegment(sketch, "E246", {"start": v(-16.75, -10.4) * mm, "end": v(-16.75, -18.02) * mm});
            skArc(sketch, "E247", {"start": v(-15.48, -14.2) * mm, "mid": v(-13.58, -12.3) * mm, "end": v(-15.48, -10.4) * mm});
            skArc(sketch, "E248", {"start": v(-15.48, -12.94) * mm, "mid": v(-14.85, -12.3) * mm, "end": v(-15.48, -11.67) * mm});
            skLineSegment(sketch, "E249", {"start": v(-15.48, -18.02) * mm, "end": v(-15.48, -14.2) * mm});
            skLineSegment(sketch, "E250", {"start": v(-16.75, -10.4) * mm, "end": v(-15.48, -10.4) * mm});
            skLineSegment(sketch, "E251", {"start": v(-16.75, -18.02) * mm, "end": v(-15.48, -18.02) * mm});
            skLineSegment(sketch, "E252", {"start": v(-15.48, -12.94) * mm, "end": v(-15.48, -11.67) * mm});
            skPoint(sketch, "E253.endSnap0", {"position": v(-12.05, -10.27) * mm});
            skLineSegment(sketch, "E254", {"start": v(-11.7, -15.36) * mm, "end": v(-11.5, -17.89) * mm});
            skLineSegment(sketch, "E255", {"start": v(-10.54, -17.89) * mm, "end": v(-11.43, -10.27) * mm});
            skLineSegment(sketch, "E256", {"start": v(-12.76, -17.89) * mm, "end": v(-12.5, -15.36) * mm});
            skLineSegment(sketch, "E257", {"start": v(-12.05, -11.53) * mm, "end": v(-12.5, -14.35) * mm});
            skLineSegment(sketch, "E258", {"start": v(-13.68, -17.89) * mm, "end": v(-12.76, -17.89) * mm});
            skLineSegment(sketch, "E253", {"start": v(-11.7, -14.34) * mm, "end": v(-12.05, -11.53) * mm});
            skLineSegment(sketch, "E259", {"start": v(-11.5, -17.89) * mm, "end": v(-10.54, -17.89) * mm});
            skLineSegment(sketch, "E260", {"start": v(-12.66, -10.27) * mm, "end": v(-13.68, -17.89) * mm});
            skLineSegment(sketch, "E261", {"start": v(-11.43, -10.27) * mm, "end": v(-12.66, -10.27) * mm});
            skLineSegment(sketch, "E262", {"start": v(-12.5, -15.36) * mm, "end": v(-11.7, -15.36) * mm});
            skLineSegment(sketch, "E263", {"start": v(-12.5, -14.35) * mm, "end": v(-11.7, -14.34) * mm});
            skPoint(sketch, "E264.end.orphan", {"position": v(-8.35, -10.7) * mm});
            skPoint(sketch, "E265.end.orphan", {"position": v(-8.38, -10.72) * mm});
            skLineSegment(sketch, "E266", {"start": v(-6.5, -12.4) * mm, "end": v(-7.46, -12.4) * mm});
            skArc(sketch, "E267", {"start": v(-10.3, -16.2) * mm, "mid": v(-8.4, -18.1) * mm, "end": v(-6.5, -16.2) * mm});
            skLineSegment(sketch, "E268", {"start": v(-6.5, -16.2) * mm, "end": v(-7.46, -16.2) * mm});
            skArc(sketch, "E269", {"start": v(-7.46, -12.4) * mm, "mid": v(-8.4, -11.45) * mm, "end": v(-9.34, -12.4) * mm});
            skArc(sketch, "E270", {"start": v(-9.34, -16.2) * mm, "mid": v(-8.4, -17.14) * mm, "end": v(-7.46, -16.2) * mm});
            skArc(sketch, "E271", {"start": v(-6.5, -12.4) * mm, "mid": v(-8.4, -10.49) * mm, "end": v(-10.3, -12.4) * mm});
            skPoint(sketch, "E272.end.orphan", {"position": v(-8.4, -10.49) * mm});
            skLineSegment(sketch, "E273", {"start": v(-9.34, -12.4) * mm, "end": v(-9.34, -16.2) * mm});
            skLineSegment(sketch, "E274", {"start": v(-10.3, -16.2) * mm, "end": v(-10.3, -12.4) * mm});
            skLineSegment(sketch, "E275", {"start": v(-2.88, -11.57) * mm, "end": v(-2.88, -10.2) * mm});
            skLineSegment(sketch, "E276", {"start": v(-4.8, -13.38) * mm, "end": v(-4.8, -11.57) * mm});
            skLineSegment(sketch, "E277", {"start": v(-3.79, -13.38) * mm, "end": v(-4.8, -13.38) * mm});
            skLineSegment(sketch, "E278", {"start": v(-2.88, -10.2) * mm, "end": v(-6.3, -10.2) * mm});
            skLineSegment(sketch, "E279", {"start": v(-2.88, -16.72) * mm, "end": v(-4.8, -16.72) * mm});
            skLineSegment(sketch, "E280", {"start": v(-2.88, -17.82) * mm, "end": v(-2.88, -16.72) * mm});
            skLineSegment(sketch, "E281", {"start": v(-6.3, -10.2) * mm, "end": v(-6.3, -17.82) * mm});
            skLineSegment(sketch, "E282", {"start": v(-4.8, -11.57) * mm, "end": v(-2.88, -11.57) * mm});
            skLineSegment(sketch, "E283", {"start": v(-3.79, -14.8) * mm, "end": v(-3.79, -13.38) * mm});
            skLineSegment(sketch, "E284", {"start": v(-6.3, -17.82) * mm, "end": v(-2.88, -17.82) * mm});
            skLineSegment(sketch, "E285", {"start": v(-4.8, -16.72) * mm, "end": v(-4.8, -14.8) * mm});
            skLineSegment(sketch, "E286", {"start": v(-4.8, -14.8) * mm, "end": v(-3.79, -14.8) * mm});
            skArc(sketch, "E287", {"start": v(4.09, -12) * mm, "mid": v(1.66, -10.17) * mm, "end": v(0.57, -13.01) * mm});
            skLineSegment(sketch, "E288", {"start": v(1.36, -12.46) * mm, "end": v(3.71, -14.68) * mm});
            skArc(sketch, "E289", {"start": v(3.12, -12) * mm, "mid": v(1.95, -11.1) * mm, "end": v(1.36, -12.46) * mm});
            skPoint(sketch, "E290.start.orphan", {"position": v(2.18, -17.72) * mm});
            skArc(sketch, "E291", {"start": v(1.24, -15.81) * mm, "mid": v(2.44, -16.71) * mm, "end": v(2.98, -15.3) * mm});
            skArc(sketch, "E292", {"start": v(0.28, -15.81) * mm, "mid": v(2.78, -17.62) * mm, "end": v(3.71, -14.68) * mm});
            skPoint(sketch, "E293.start.orphan", {"position": v(2.18, -10.1) * mm});
            skLineSegment(sketch, "E294", {"start": v(0.57, -13.01) * mm, "end": v(2.98, -15.3) * mm});
            skLineSegment(sketch, "E295", {"start": v(4.09, -12) * mm, "end": v(3.12, -12) * mm});
            skLineSegment(sketch, "E296", {"start": v(0.28, -15.81) * mm, "end": v(1.24, -15.81) * mm});
            skPoint(sketch, "E297.end.orphan", {"position": v(6.1, -11.03) * mm});
            skPoint(sketch, "E298.end.orphan", {"position": v(6.12, -11.27) * mm});
            skPoint(sketch, "E299.end.orphan", {"position": v(6.15, -11.24) * mm});
            skPoint(sketch, "E300.end.orphan", {"position": v(6.1, -11) * mm});
            skPoint(sketch, "E301.end.orphan", {"position": v(6.13, -11.23) * mm});
            skPoint(sketch, "E302.end.orphan", {"position": v(6.15, -11.2) * mm});
            skLineSegment(sketch, "E303", {"start": v(8, -12.03) * mm, "end": v(7.04, -12.03) * mm});
            skArc(sketch, "E304", {"start": v(7.04, -12.03) * mm, "mid": v(6.1, -11.1) * mm, "end": v(5.16, -12.03) * mm});
            skArc(sketch, "E305", {"start": v(4.2, -15.84) * mm, "mid": v(6.1, -17.75) * mm, "end": v(8, -15.84) * mm});
            skPoint(sketch, "E306.end.orphan", {"position": v(6.1, -10.13) * mm});
            skArc(sketch, "E307", {"start": v(8, -12.03) * mm, "mid": v(6.1, -10.13) * mm, "end": v(4.2, -12.03) * mm});
            skLineSegment(sketch, "E308", {"start": v(5.16, -12.03) * mm, "end": v(5.16, -15.84) * mm});
            skPoint(sketch, "E309.end.orphan", {"position": v(6.12, -10.37) * mm});
            skArc(sketch, "E310", {"start": v(5.16, -15.84) * mm, "mid": v(6.1, -16.78) * mm, "end": v(7.04, -15.84) * mm});
            skLineSegment(sketch, "E311", {"start": v(8, -15.84) * mm, "end": v(7.04, -15.84) * mm});
            skPoint(sketch, "E312.end.orphan", {"position": v(6.15, -10.34) * mm});
            skLineSegment(sketch, "E313", {"start": v(4.2, -15.84) * mm, "end": v(4.2, -12.03) * mm});
            skLineSegment(sketch, "E314", {"start": v(11.47, -17.66) * mm, "end": v(8.32, -17.66) * mm});
            skLineSegment(sketch, "E315", {"start": v(11.47, -15.93) * mm, "end": v(11.47, -17.66) * mm});
            skLineSegment(sketch, "E316", {"start": v(10.43, -15.93) * mm, "end": v(11.47, -15.93) * mm});
            skLineSegment(sketch, "E317", {"start": v(9.32, -15.93) * mm, "end": v(9.32, -11.95) * mm});
            skLineSegment(sketch, "E318", {"start": v(10.43, -11.95) * mm, "end": v(10.43, -15.93) * mm});
            skLineSegment(sketch, "E319", {"start": v(8.32, -11.95) * mm, "end": v(8.32, -10.04) * mm});
            skLineSegment(sketch, "E320", {"start": v(9.32, -11.95) * mm, "end": v(8.32, -11.95) * mm});
            skLineSegment(sketch, "E321", {"start": v(8.32, -10.04) * mm, "end": v(11.47, -10.04) * mm});
            skLineSegment(sketch, "E322", {"start": v(8.32, -17.66) * mm, "end": v(8.32, -15.93) * mm});
            skLineSegment(sketch, "E323", {"start": v(8.32, -15.93) * mm, "end": v(9.32, -15.93) * mm});
            skLineSegment(sketch, "E324", {"start": v(11.47, -11.95) * mm, "end": v(10.43, -11.95) * mm});
            skLineSegment(sketch, "E325", {"start": v(11.47, -10.04) * mm, "end": v(11.47, -11.95) * mm});
            skLineSegment(sketch, "E326", {"start": v(11.78, -17.6) * mm, "end": v(15.2, -17.6) * mm});
            skLineSegment(sketch, "E327", {"start": v(15.2, -16.51) * mm, "end": v(13.27, -16.51) * mm});
            skLineSegment(sketch, "E328", {"start": v(13.27, -16.51) * mm, "end": v(13.27, -14.59) * mm});
            skLineSegment(sketch, "E329", {"start": v(13.27, -11.36) * mm, "end": v(15.2, -11.36) * mm});
            skLineSegment(sketch, "E330", {"start": v(15.2, -9.99) * mm, "end": v(11.78, -9.99) * mm});
            skLineSegment(sketch, "E331", {"start": v(13.27, -13.17) * mm, "end": v(13.27, -11.36) * mm});
            skLineSegment(sketch, "E332", {"start": v(11.78, -9.99) * mm, "end": v(11.78, -17.6) * mm});
            skLineSegment(sketch, "E333", {"start": v(13.27, -14.59) * mm, "end": v(14.3, -14.59) * mm});
            skLineSegment(sketch, "E334", {"start": v(14.3, -14.59) * mm, "end": v(14.3, -13.17) * mm});
            skLineSegment(sketch, "E335", {"start": v(15.2, -17.6) * mm, "end": v(15.2, -16.51) * mm});
            skLineSegment(sketch, "E336", {"start": v(14.3, -13.17) * mm, "end": v(13.27, -13.17) * mm});
            skLineSegment(sketch, "E337", {"start": v(15.2, -11.36) * mm, "end": v(15.2, -9.99) * mm});
            skLineSegment(sketch, "E338", {"start": v(17.62, -13.92) * mm, "end": v(17.62, -17.73) * mm});
            skLineSegment(sketch, "E339", {"start": v(20.67, -10.11) * mm, "end": v(19.4, -10.11) * mm});
            skLineSegment(sketch, "E340", {"start": v(16.35, -10.11) * mm, "end": v(16.35, -17.73) * mm});
            skLineSegment(sketch, "E341", {"start": v(16.35, -17.73) * mm, "end": v(17.62, -17.73) * mm});
            skLineSegment(sketch, "E342", {"start": v(17.62, -13.92) * mm, "end": v(19.4, -17.73) * mm});
            skLineSegment(sketch, "E343", {"start": v(17.62, -10.11) * mm, "end": v(19.4, -13.92) * mm});
            skLineSegment(sketch, "E344", {"start": v(16.35, -10.11) * mm, "end": v(17.62, -10.11) * mm});
            skLineSegment(sketch, "E345", {"start": v(20.67, -17.73) * mm, "end": v(20.67, -10.11) * mm});
            skLineSegment(sketch, "E346", {"start": v(19.4, -10.11) * mm, "end": v(19.4, -13.92) * mm});
            skLineSegment(sketch, "E347", {"start": v(19.4, -17.73) * mm, "end": v(20.67, -17.73) * mm});
            skPoint(sketch, "E348.end.orphan", {"position": v(22.93, -10.61) * mm});
            skPoint(sketch, "E349.end.orphan", {"position": v(22.99, -10.82) * mm});
            skPoint(sketch, "E350.end.orphan", {"position": v(22.93, -11.52) * mm});
            skPoint(sketch, "E351.end.orphan", {"position": v(22.99, -11.69) * mm});
            skPoint(sketch, "E352.end.orphan", {"position": v(22.96, -11.71) * mm});
            skPoint(sketch, "E353.end.orphan", {"position": v(22.96, -10.85) * mm});
            skPoint(sketch, "E354.end.orphan", {"position": v(22.94, -11.48) * mm});
            skPoint(sketch, "E355.end.orphan", {"position": v(22.98, -11.73) * mm});
            skPoint(sketch, "E356.end.orphan", {"position": v(22.96, -11.75) * mm});
            skArc(sketch, "E357", {"start": v(21, -15.7) * mm, "mid": v(22.9, -17.61) * mm, "end": v(24.81, -15.7) * mm});
            skPoint(sketch, "E358.end.orphan", {"position": v(22.9, -10) * mm});
            skArc(sketch, "E359", {"start": v(21.97, -15.7) * mm, "mid": v(22.9, -16.65) * mm, "end": v(23.85, -15.7) * mm});
            skPoint(sketch, "E360.end.orphan", {"position": v(22.96, -10.2) * mm});
            skLineSegment(sketch, "E361", {"start": v(24.81, -11.9) * mm, "end": v(23.85, -11.9) * mm});
            skArc(sketch, "E362", {"start": v(23.85, -11.9) * mm, "mid": v(22.9, -10.96) * mm, "end": v(21.97, -11.9) * mm});
            skLineSegment(sketch, "E363", {"start": v(21.97, -11.9) * mm, "end": v(21.97, -15.7) * mm});
            skLineSegment(sketch, "E364", {"start": v(24.81, -15.7) * mm, "end": v(23.85, -15.7) * mm});
            skPoint(sketch, "E365.end.orphan", {"position": v(22.9, -10.9) * mm});
            skArc(sketch, "E366", {"start": v(24.81, -11.9) * mm, "mid": v(22.9, -10) * mm, "end": v(21, -11.9) * mm});
            skPoint(sketch, "E367.end.orphan", {"position": v(22.96, -11.06) * mm});
            skPoint(sketch, "E368.end.orphan", {"position": v(22.93, -11.1) * mm});
            skPoint(sketch, "E369.end.orphan", {"position": v(22.93, -10.23) * mm});
            skPoint(sketch, "E370.end.orphan", {"position": v(22.9, -10.85) * mm});
            skPoint(sketch, "E371.end.orphan", {"position": v(22.96, -11.1) * mm});
            skPoint(sketch, "E372.end.orphan", {"position": v(22.93, -11.13) * mm});
            skLineSegment(sketch, "E373", {"start": v(21, -15.7) * mm, "end": v(21, -11.9) * mm});
            skLineSegment(sketch, "E374", {"start": v(28.61, -9.99) * mm, "end": v(25.19, -9.99) * mm});
            skLineSegment(sketch, "E375", {"start": v(25.19, -9.99) * mm, "end": v(25.19, -17.6) * mm});
            skLineSegment(sketch, "E376", {"start": v(26.68, -16.51) * mm, "end": v(26.68, -14.58) * mm});
            skLineSegment(sketch, "E377", {"start": v(26.68, -14.58) * mm, "end": v(27.7, -14.58) * mm});
            skLineSegment(sketch, "E378", {"start": v(27.7, -14.58) * mm, "end": v(27.7, -13.17) * mm});
            skLineSegment(sketch, "E379", {"start": v(25.19, -17.6) * mm, "end": v(28.61, -17.6) * mm});
            skLineSegment(sketch, "E380", {"start": v(28.61, -11.36) * mm, "end": v(28.61, -9.99) * mm});
            skLineSegment(sketch, "E381", {"start": v(26.68, -13.17) * mm, "end": v(26.68, -11.36) * mm});
            skLineSegment(sketch, "E382", {"start": v(26.68, -11.36) * mm, "end": v(28.61, -11.36) * mm});
            skLineSegment(sketch, "E383", {"start": v(28.61, -16.51) * mm, "end": v(26.68, -16.51) * mm});
            skLineSegment(sketch, "E384", {"start": v(28.61, -17.6) * mm, "end": v(28.61, -16.51) * mm});
            skLineSegment(sketch, "E385", {"start": v(27.7, -13.17) * mm, "end": v(26.68, -13.17) * mm});
            skSolve(sketch);
        }
        {
            var Q0;
            Q0 = qSketchRegion(id + "F18", true);
            extrude(context, id + "F19", {"entities" : qUnion([Q0]), "operationType" : NewBodyOperationType.REMOVE, "oppositeDirection" : true, "depth" : 2.54 * mm});
        }
    });
